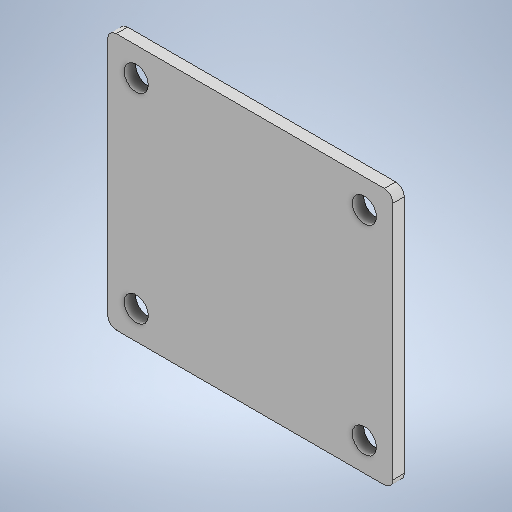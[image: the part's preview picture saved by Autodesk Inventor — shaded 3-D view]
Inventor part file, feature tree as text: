
AUTODESK INVENTOR PART (.ipt)
format: ipt  version: 2025 (Build 290162010, 162A)  size: 266,240 bytes
history: native  units: mm
features: sketch x2, other x2, sheet_metal_op x1, hole x1, chamfer x1, mirror x1
ambient origin geometry x8: Origin, YZ Plane, XZ Plane, XY Plane, X Axis, Y Axis, Z Axis, Center Point
bodies: Solid1 (feature_tree)
feature tree (8):
  sheet_metal_op  "Face1"
  hole  "Hole1"  [1 undecoded]
  chamfer  "Corner Round1"
  mirror  "Mirror1"
  sketch  "Sketch1"  dims[d0=200.0mm d1=180.0mm]
  other  "Plate1"
  sketch  "Sketch2"  dims[d2=8.0mm d3=17.0mm d4=6.0mm d5=4.0mm d6=2.0mm d7=90.0deg d8=8.0mm d9=20.594885mm d10=20.0mm d12=20.0mm d13=6.0mm]
  other  "Definition1"
note: 1 required parameter value undecoded (feature->parameter linkage not recoverable at this tier; creation-order binding heuristic only, values carry confidence <= 0.55)
